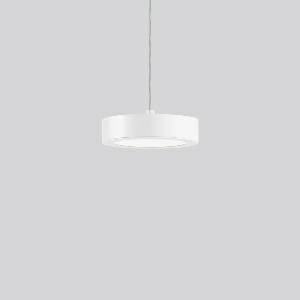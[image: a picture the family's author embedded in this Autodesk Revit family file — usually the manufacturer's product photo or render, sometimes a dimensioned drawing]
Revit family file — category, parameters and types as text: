
# Revit family: toledo_flat_round_p_901685_002_76_574d
name_source: partatom
category: Lighting Fixtures
units: mm (PartAtom-declared; Revit-internal decimal feet)

## family parameters
Cut with Voids When Loaded = No
Host = Face
Light Source = No
Part Type = Normal
Room Calculation Point = No
Round Connector Dimension = Use Diameter
Shared = No

## types (1)
- TOLEDO FLAT round P (1 x LED Modul 830, 1650 lm, 3000)
    Apparent Load = 17 VA
    CIE Flux Codes = 48 79 96 100 100
    Color Rendering = 80
    Color Temperature = 3000
    Default Elevation = 1800 mm
    Description = Series: TOLEDO FLAT
Flat cylindrical pendant luminaire. Cylinder housing sheet steel, powder-coated. Housing: die cast aluminium and sheet steel, powder-coated. Bezel ring: die-cast aluminium, powder-coated. Canopy: sheet steel, powder-coated. Lightguide and diffuser made of non-yellowing plastic (PMMA) opal matt. Suitable for pendant. Transparent suspension cable 2 m, can be shortened. Mounting rings for retrofitting a fabric lampshade available as accessory. 
Colour: white
Diameter: 257 mm
Height: 88.8 mm
Suspension length: 2000 mm
Lamp: LED
Socket: without socket
Colour temperature: 3000K
Colour rendering index (CRI): 80
System power: 17 W
Rated luminous flux: 1650 lm
Luminous efficiency: 97 lm/W
Control gear: Converter, dimmable, DALI
Protection class: I
Type of protection: IP 20
    Height = 89 mm
    Lamp = 1 x LED Modul 830
    Lamp Light Flux = 1650 lm
    Lamp count = 1
    Length = 257 mm
    Lifetime = 50000 h
    Luminous efficacy = 97 lm/W
    Manufacturer = RZB
    ModVariant = No
    Model = 901685.002.76
    Mounting Place = Ceiling
    Mounting Type = Pendant
    Number of Poles = 1
    OnlyDefault = Yes
    Power Factor = 1
    Product Name = TOLEDO FLAT round P
    Product group = Pendant luminaires
    ProductGroupID = 902
    Protection Class = Protection class I
    Protection Degree = IP 20
    RLX_Detail_Level = 1
    RLX_Emergency_Light_Flux = 0 lm
    RLX_Emergency_Type = 0
    RLX_Emergency_Type_DB = No
    RlxData = <blob elided: 69905 chars, md5=08c46ed5>
    Socket = socket
    Standby Power = 0 W
    System Light Flux = 1650 lm
    System Power = 17 W
    Type Comments = Product without accessories
    Type Image = 901685.002.jpg
    URL = http://relux.com
    VarID = ---
    Voltage = 230 V
    Voltage Range = 220-240 V
    Weight = 0.00 kg
    Width = 0 mm  [stored 0 ft]

note: [stored X ft] marks values corroborated as IEEE doubles in the binary element streams (Revit-internal decimal feet)

## geometry (parser evidence)
native form markers: Blend x4, Sweep x11
no freeform markers — native parametric forms only
